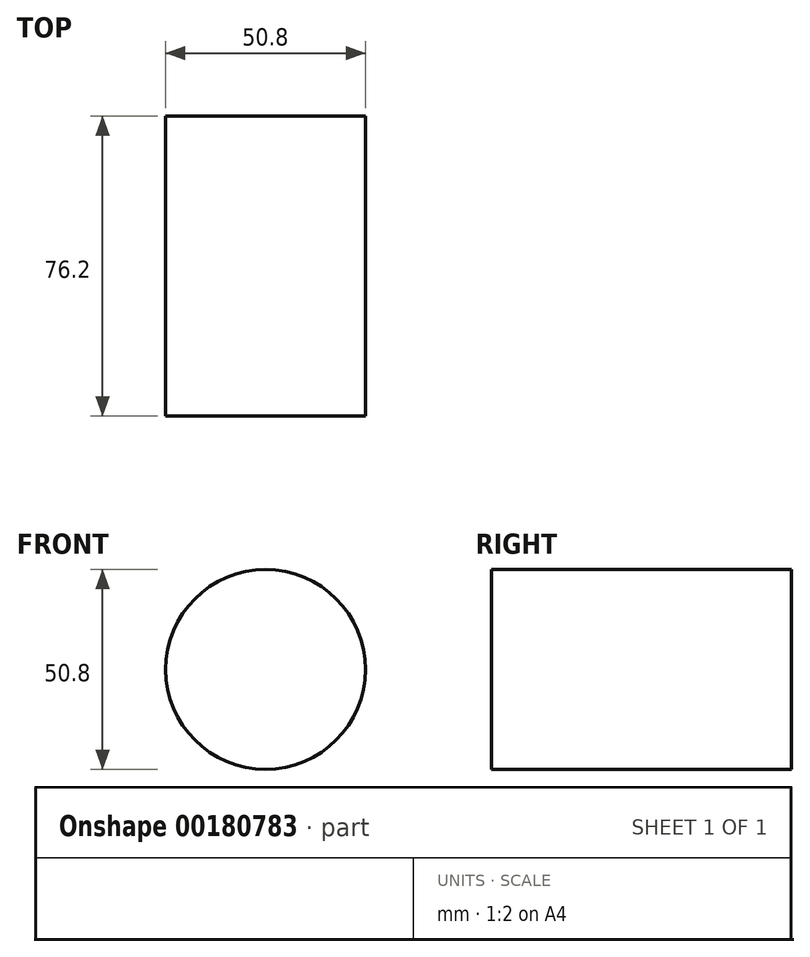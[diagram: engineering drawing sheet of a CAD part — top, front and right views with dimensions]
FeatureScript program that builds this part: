
annotation { "Feature Type Name" : "Feature", "Feature Type Description" : "" }
export const myFeature = defineFeature(function(context is Context, id is Id, definition is map)
    precondition{}
    {
        {
            var Q0;
            Q0=qCreatedBy(makeId("Front.planeOp"),FACE);
            var sketch = newSketch(context, id + "F0", { "sketchPlane" : qUnion([Q0])});
            skCircle(sketch, "E0", {"center": v(0, 0) * mm, "radius": 25.4 * mm});
            skSolve(sketch);
        }
        {
            var Q0;
            Q0=sQuery(id+"F0.wireOp",EDGE,"E0");
            extrude(context, id + "F1", {"bodyType" : ToolBodyType.SURFACE, "surfaceEntities" : qUnion([Q0]), "depth" : 76.2 * mm});
        }
    });
